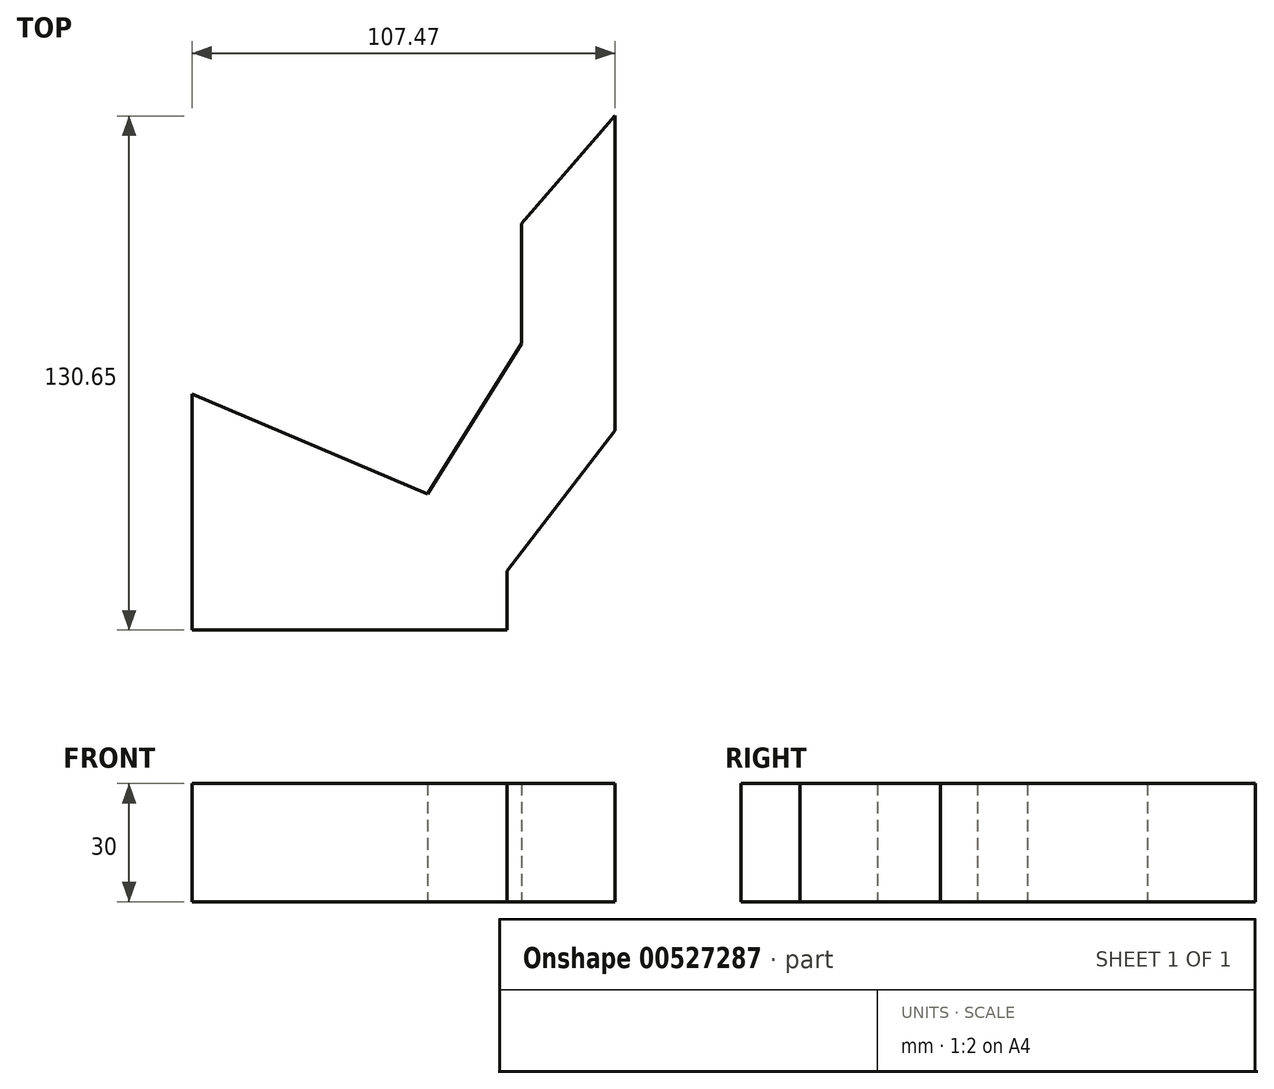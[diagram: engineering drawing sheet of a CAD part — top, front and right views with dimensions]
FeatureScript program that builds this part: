
annotation { "Feature Type Name" : "Feature", "Feature Type Description" : "" }
export const myFeature = defineFeature(function(context is Context, id is Id, definition is map)
    precondition{}
    {
        {
            var Q0;
            Q0=qCreatedBy(makeId("Top.planeOp"),FACE);
            var sketch = newSketch(context, id + "F0", { "sketchPlane" : qUnion([Q0])});
            skLineSegment(sketch, "E0", {"start": v(-113.48, -9.73) * mm, "end": v(-113.48, -69.73) * mm});
            skLineSegment(sketch, "E1", {"start": v(-113.48, -69.73) * mm, "end": v(-33.48, -69.73) * mm});
            skLineSegment(sketch, "E2", {"start": v(-33.48, -69.73) * mm, "end": v(-33.48, -54.73) * mm});
            skLineSegment(sketch, "E3", {"start": v(-33.48, -54.73) * mm, "end": v(-6.01, -19.08) * mm});
            skLineSegment(sketch, "E4", {"start": v(-6.01, -19.08) * mm, "end": v(-6.01, 60.92) * mm});
            skLineSegment(sketch, "E5", {"start": v(-6.01, 60.92) * mm, "end": v(-29.8, 33.56) * mm});
            skLineSegment(sketch, "E6", {"start": v(-29.8, 33.56) * mm, "end": v(-29.8, 3.04) * mm});
            skLineSegment(sketch, "E7", {"start": v(-29.8, 3.04) * mm, "end": v(-53.64, -35.12) * mm});
            skLineSegment(sketch, "E8", {"start": v(-53.64, -35.12) * mm, "end": v(-113.48, -9.73) * mm});
            skSolve(sketch);
        }
        {
            var Q0;
            Q0 = qSketchRegion(id + "F0", true);
            extrude(context, id + "F1", {"entities" : qUnion([Q0]), "depth" : 30 * mm, "offsetDistance" : 25 * mm});
        }
    });
